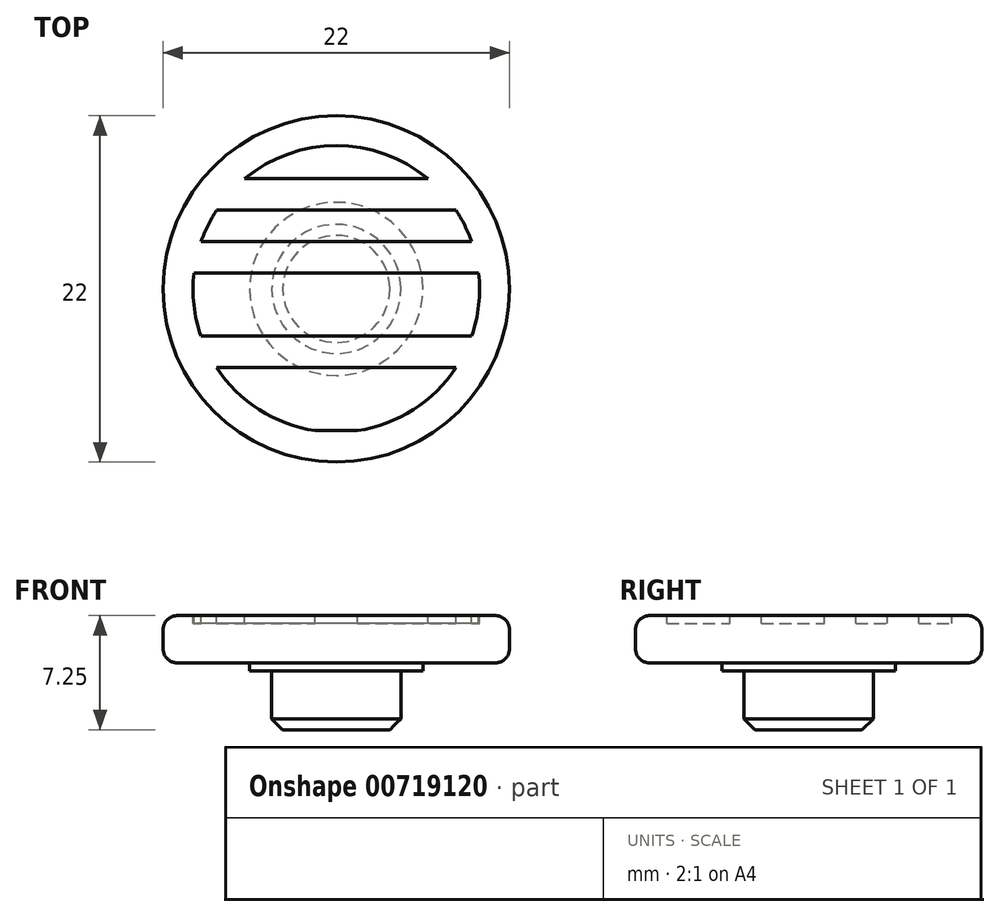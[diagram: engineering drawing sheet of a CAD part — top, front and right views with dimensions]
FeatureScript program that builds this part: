
annotation { "Feature Type Name" : "Feature", "Feature Type Description" : "" }
export const myFeature = defineFeature(function(context is Context, id is Id, definition is map)
    precondition{}
    {
        {
            var Q0;
            Q0=qCreatedBy(makeId("Top.planeOp"),FACE);
            var sketch = newSketch(context, id + "F0", { "sketchPlane" : qUnion([Q0])});
            skCircle(sketch, "E0", {"center": v(0, 0) * mm, "radius": 4.1 * mm});
            skCircle(sketch, "E1", {"center": v(0, 0) * mm, "radius": 11 * mm});
            skCircle(sketch, "E2", {"center": v(0, 0) * mm, "radius": 5.5 * mm});
            skSolve(sketch);
        }
        {
            var Q0;
            Q0=makeQuery(id+"F0.imprint","IMPRINT",FACE,{"disambiguationData":[TD([[makeQuery(id+"F0.imprint","IMPRINT",EDGE,{"derivedFrom":sQuery(id+"F0.wireOp",EDGE,"E0")}),-1.0]])]});
            var Q1;
            Q1=makeQuery(id+"F0.imprint","IMPRINT",FACE,{"disambiguationData":[TD([[makeQuery(id+"F0.imprint","IMPRINT",EDGE,{"derivedFrom":sQuery(id+"F0.wireOp",EDGE,"E0")}),1.0]])]});
            var Q2;
            Q2=makeQuery(id+"F0.imprint","IMPRINT",FACE,{"disambiguationData":[TD([[makeQuery(id+"F0.imprint","IMPRINT",EDGE,{"derivedFrom":sQuery(id+"F0.wireOp",EDGE,"E1")}),1.0]])]});
            extrude(context, id + "F1", {"entities" : qUnion([Q0, Q1, Q2]), "depth" : 3 * mm, "offsetDistance" : 25 * mm});
        }
        {
            var Q0;
            Q0=makeQuery(id+"F0.imprint","IMPRINT",FACE,{"disambiguationData":[TD([[makeQuery(id+"F0.imprint","IMPRINT",EDGE,{"derivedFrom":sQuery(id+"F0.wireOp",EDGE,"E0")}),1.0]])]});
            extrude(context, id + "F2", {"entities" : qUnion([Q0]), "operationType" : NewBodyOperationType.ADD, "oppositeDirection" : true, "depth" : 4.25 * mm, "offsetDistance" : 25 * mm});
        }
        {
            var Q0;
            Q0=makeQuery(id+"F2.opExtrude","CAP_FACE",FACE,{"disambiguationData":[OSD([sQuery(id+"F0.wireOp",EDGE,"E0")])],"isStart":false});
            chamfer(context, id + "F3", {"entities" : qUnion([Q0]), "width" : 0.7 * mm});
        }
        {
            var Q0;
            Q0=makeQuery(id+"F1.opExtrude","SWEPT_FACE",FACE,{"disambiguationData":[OSD([sQuery(id+"F0.wireOp",EDGE,"E1")])]});
            fillet(context, id + "F4", {"entities" : qUnion([Q0]), "radius" : 0.9 * mm, "allowEdgeOverflow" : false});
        }
        {
            var Q0;
            Q0=makeQuery(id+"F0.imprint","IMPRINT",FACE,{"disambiguationData":[TD([[makeQuery(id+"F0.imprint","IMPRINT",EDGE,{"derivedFrom":sQuery(id+"F0.wireOp",EDGE,"E0")}),-1.0]])]});
            extrude(context, id + "F5", {"entities" : qUnion([Q0]), "operationType" : NewBodyOperationType.ADD, "oppositeDirection" : true, "depth" : .5 * mm, "offsetDistance" : 25 * mm});
        }
        {
            var Q0;
            Q0=makeQuery(id+"F1.opExtrude","CAP_FACE",FACE,{"disambiguationData":[OSD([sQuery(id+"F0.wireOp",EDGE,"E1")])],"isStart":false});
            var sketch = newSketch(context, id + "F6", { "sketchPlane" : qUnion([Q0])});
            skCircle(sketch, "E3.0", {"center": v(0, 0) * mm, "radius": 9.1 * mm});
            skLineSegment(sketch, "E4.bottom", {"start": v(15.2, 1) * mm, "end": v(-15.2, 1) * mm});
            skLineSegment(sketch, "E4.top", {"start": v(15.2, -1) * mm, "end": v(-15.2, -1) * mm});
            skLineSegment(sketch, "E4.left", {"start": v(15.2, 1) * mm, "end": v(15.2, -1) * mm, "construction": true});
            skLineSegment(sketch, "E4.right", {"start": v(-15.2, 1) * mm, "end": v(-15.2, -1) * mm, "construction": true});
            skLineSegment(sketch, "E5.0.1.0", {"start": v(15.2, 3) * mm, "end": v(-15.2, 3) * mm});
            skLineSegment(sketch, "E5.0.1.1", {"start": v(15.2, 5) * mm, "end": v(-15.2, 5) * mm});
            skLineSegment(sketch, "E5.0.2.0", {"start": v(15.2, 7) * mm, "end": v(-15.2, 7) * mm});
            skLineSegment(sketch, "E5.0.2.1", {"start": v(15.2, 9) * mm, "end": v(-15.2, 9) * mm});
            skLineSegment(sketch, "E5.direction2", {"start": v(-15.2, -1) * mm, "end": v(-15.2, 3) * mm, "construction": true});
            skLineSegment(sketch, "E6.0.1.0", {"start": v(15.2, -5) * mm, "end": v(-15.2, -5) * mm});
            skLineSegment(sketch, "E6.0.1.1", {"start": v(15.2, -3) * mm, "end": v(-15.2, -3) * mm});
            skLineSegment(sketch, "E6.0.2.0", {"start": v(15.2, -9) * mm, "end": v(-15.2, -9) * mm});
            skLineSegment(sketch, "E6.0.2.1", {"start": v(15.2, -7) * mm, "end": v(-15.2, -7) * mm});
            skLineSegment(sketch, "E6.direction1", {"start": v(-15.2, -1) * mm, "end": v(9.8, -1) * mm, "construction": true});
            skLineSegment(sketch, "E6.direction2", {"start": v(-15.2, -1) * mm, "end": v(-15.2, -5) * mm, "construction": true});
            skSolve(sketch);
        }
        {
            var Q0;
            {var subQ0=sQuery(id+"F6.wireOp",EDGE,"E6.0.2.1");var subQ1=sQuery(id+"F6.wireOp",EDGE,"E3.0");var subQ2=makeQuery(id+"F6.imprint","INTERSECT",VERTEX,{"disambiguationData":[OD(0.0)],"derivedFrom":[subQ1,subQ0]});Q0=makeQuery(id+"F6.imprint","IMPRINT",FACE,{"disambiguationData":[TD([[makeQuery(id+"F6.imprint","IMPRINT",EDGE,{"disambiguationData":[TD([[subQ2,-1.0]])],"derivedFrom":subQ1}),1.0]])]});}
            var Q1;
            {var subQ0=sQuery(id+"F6.wireOp",EDGE,"E6.0.1.1");var subQ1=sQuery(id+"F6.wireOp",EDGE,"E3.0");var subQ2=makeQuery(id+"F6.imprint","INTERSECT",VERTEX,{"disambiguationData":[OD(0.0)],"derivedFrom":[subQ1,subQ0]});Q1=makeQuery(id+"F6.imprint","IMPRINT",FACE,{"disambiguationData":[TD([[makeQuery(id+"F6.imprint","IMPRINT",EDGE,{"disambiguationData":[TD([[subQ2,-1.0]])],"derivedFrom":subQ1}),1.0]])]});}
            var Q2;
            {var subQ0=sQuery(id+"F6.wireOp",EDGE,"E4.bottom");var subQ1=sQuery(id+"F6.wireOp",EDGE,"E3.0");var subQ2=makeQuery(id+"F6.imprint","INTERSECT",VERTEX,{"disambiguationData":[OD(1.0)],"derivedFrom":[subQ1,subQ0]});Q2=makeQuery(id+"F6.imprint","IMPRINT",FACE,{"disambiguationData":[TD([[makeQuery(id+"F6.imprint","IMPRINT",EDGE,{"disambiguationData":[TD([[subQ2,-1.0]])],"derivedFrom":subQ1}),1.0]])]});}
            var Q3;
            {var subQ0=sQuery(id+"F6.wireOp",EDGE,"E5.0.1.0");var subQ1=sQuery(id+"F6.wireOp",EDGE,"E3.0");var subQ2=makeQuery(id+"F6.imprint","INTERSECT",VERTEX,{"disambiguationData":[OD(0.0)],"derivedFrom":[subQ1,subQ0]});Q3=makeQuery(id+"F6.imprint","IMPRINT",FACE,{"disambiguationData":[TD([[makeQuery(id+"F6.imprint","IMPRINT",EDGE,{"disambiguationData":[TD([[subQ2,-1.0]])],"derivedFrom":subQ1}),1.0]])]});}
            var Q4;
            {var subQ0=sQuery(id+"F6.wireOp",EDGE,"E5.0.2.0");var subQ1=sQuery(id+"F6.wireOp",EDGE,"E3.0");var subQ2=makeQuery(id+"F6.imprint","INTERSECT",VERTEX,{"disambiguationData":[OD(0.0)],"derivedFrom":[subQ1,subQ0]});Q4=makeQuery(id+"F6.imprint","IMPRINT",FACE,{"disambiguationData":[TD([[makeQuery(id+"F6.imprint","IMPRINT",EDGE,{"disambiguationData":[TD([[subQ2,-1.0]])],"derivedFrom":subQ1}),1.0]])]});}
            var Q5;
            {var subQ0=sQuery(id+"F6.wireOp",EDGE,"E6.0.2.0");var subQ1=sQuery(id+"F6.wireOp",EDGE,"E3.0");var subQ2=makeQuery(id+"F6.imprint","INTERSECT",VERTEX,{"disambiguationData":[OD(0.0)],"derivedFrom":[subQ1,subQ0]});Q5=makeQuery(id+"F6.imprint","IMPRINT",FACE,{"disambiguationData":[TD([[makeQuery(id+"F6.imprint","IMPRINT",EDGE,{"disambiguationData":[TD([[subQ2,-1.0]])],"derivedFrom":subQ1}),1.0]])]});}
            var Q6;
            {var subQ0=sQuery(id+"F6.wireOp",EDGE,"E5.0.2.1");var subQ1=sQuery(id+"F6.wireOp",EDGE,"E3.0");var subQ2=makeQuery(id+"F6.imprint","INTERSECT",VERTEX,{"disambiguationData":[OD(0.0)],"derivedFrom":[subQ1,subQ0]});Q6=makeQuery(id+"F6.imprint","IMPRINT",FACE,{"disambiguationData":[TD([[makeQuery(id+"F6.imprint","IMPRINT",EDGE,{"disambiguationData":[TD([[subQ2,-1.0]])],"derivedFrom":subQ1}),1.0]])]});}
            extrude(context, id + "F7", {"entities" : qUnion([Q0, Q1, Q2, Q3, Q4, Q5, Q6]), "operationType" : NewBodyOperationType.REMOVE, "oppositeDirection" : true, "depth" : .5 * mm, "offsetDistance" : 25 * mm});
        }
    });
